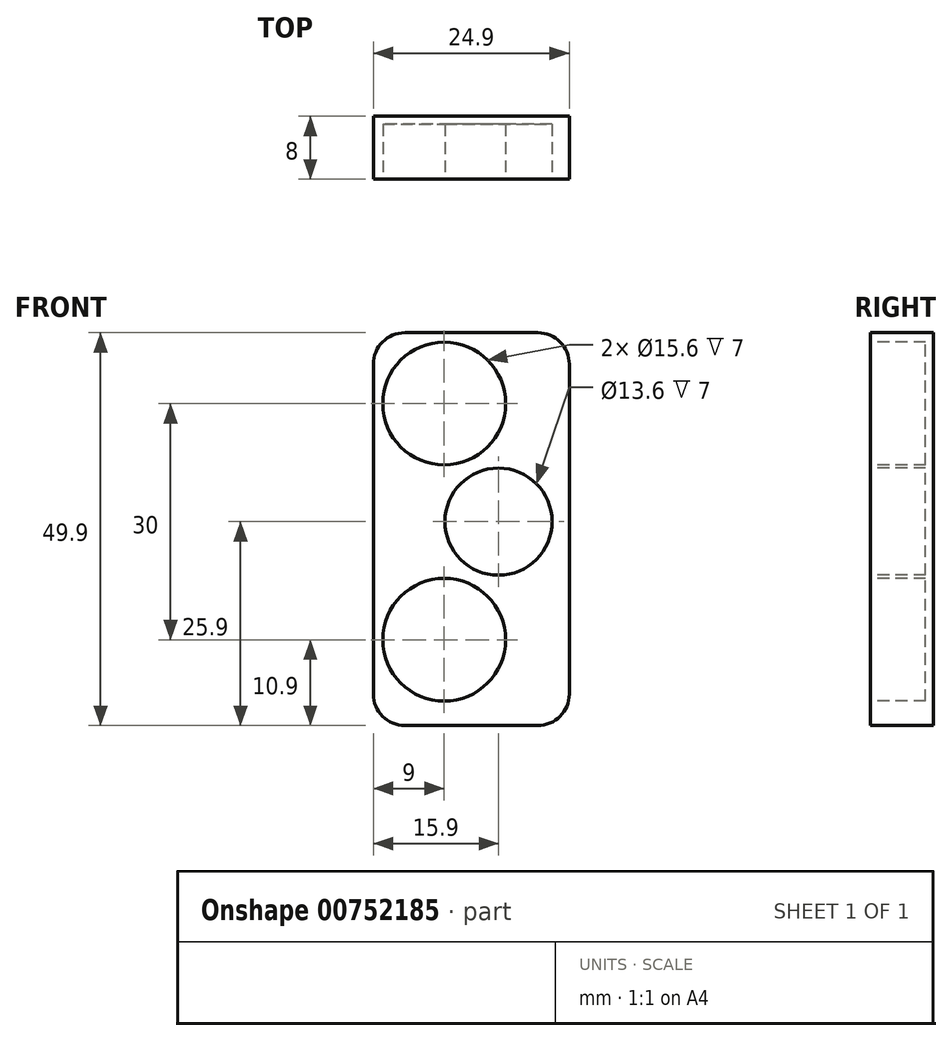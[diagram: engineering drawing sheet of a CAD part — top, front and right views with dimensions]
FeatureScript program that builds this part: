
annotation { "Feature Type Name" : "Feature", "Feature Type Description" : "" }
export const myFeature = defineFeature(function(context is Context, id is Id, definition is map)
    precondition{}
    {
        {
            var Q0;
            Q0=qCreatedBy(makeId("Front.planeOp"),FACE);
            var sketch = newSketch(context, id + "F0", { "sketchPlane" : qUnion([Q0])});
            skLineSegment(sketch, "E0.bottom", {"start": v(4, 0) * mm, "end": v(20.9, 0) * mm});
            skLineSegment(sketch, "E0.top", {"start": v(4, -49.9) * mm, "end": v(20.9, -49.9) * mm});
            skLineSegment(sketch, "E0.left", {"start": v(0, -4) * mm, "end": v(0, -45.9) * mm});
            skLineSegment(sketch, "E0.right", {"start": v(24.9, -4) * mm, "end": v(24.9, -45.9) * mm});
            skPoint(sketch, "E1.visualSharp", {"position": v(0, 0) * mm});
            skArc(sketch, "E1.filletArc", {"start": v(4, 0) * mm, "mid": v(1.17, -1.17) * mm, "end": v(0, -4) * mm});
            skPoint(sketch, "E2.visualSharp", {"position": v(24.9, 0) * mm});
            skArc(sketch, "E2.filletArc", {"start": v(24.9, -4) * mm, "mid": v(23.73, -1.17) * mm, "end": v(20.9, 0) * mm});
            skPoint(sketch, "E3.visualSharp", {"position": v(0, -49.9) * mm});
            skArc(sketch, "E3.filletArc", {"start": v(0, -45.9) * mm, "mid": v(1.17, -48.73) * mm, "end": v(4, -49.9) * mm});
            skPoint(sketch, "E4.visualSharp", {"position": v(24.9, -49.9) * mm});
            skArc(sketch, "E4.filletArc", {"start": v(20.9, -49.9) * mm, "mid": v(23.73, -48.73) * mm, "end": v(24.9, -45.9) * mm});
            skSolve(sketch);
        }
        {
            var Q0;
            Q0 = qSketchRegion(id + "F0", true);
            extrude(context, id + "F1", {"entities" : qUnion([Q0]), "depth" : 8 * mm, "offsetDistance" : 25 * mm});
        }
        {
            var Q0;
            Q0=makeQuery(id+"F1.opExtrude","CAP_FACE",FACE,{"disambiguationData":[OSD([sQuery(id+"F0.wireOp",EDGE,"E0.bottom"),sQuery(id+"F0.wireOp",EDGE,"E0.top"),sQuery(id+"F0.wireOp",EDGE,"E0.left"),sQuery(id+"F0.wireOp",EDGE,"E0.right"),sQuery(id+"F0.wireOp",EDGE,"E1.filletArc"),sQuery(id+"F0.wireOp",EDGE,"E2.filletArc"),sQuery(id+"F0.wireOp",EDGE,"E3.filletArc"),sQuery(id+"F0.wireOp",EDGE,"E4.filletArc")])],"isStart":false});
            var sketch = newSketch(context, id + "F2", { "sketchPlane" : qUnion([Q0])});
            skCircle(sketch, "E5", {"center": v(9, -9) * mm, "radius": 7.8 * mm});
            skCircle(sketch, "E6", {"center": v(15.9, -24) * mm, "radius": 6.8 * mm});
            skCircle(sketch, "E7", {"center": v(9, -39) * mm, "radius": 7.8 * mm});
            skSolve(sketch);
        }
        {
            var Q0;
            Q0 = qSketchRegion(id + "F2", true);
            extrude(context, id + "F3", {"entities" : qUnion([Q0]), "operationType" : NewBodyOperationType.REMOVE, "oppositeDirection" : true, "depth" : 7 * mm, "offsetDistance" : 25 * mm});
        }
    });
